# Revit family: Edge_TB42_E_Side_Hung_Standard
name_source: partatom
category: Windows
revit_build: Autodesk Revit 2014 (Build: 20130308_1515(x64)
units: mm (PartAtom-declared; Revit-internal decimal feet)

## types (18) — shared parameters
Aluminium Thickness = 1 mm  [stored 0.00328084 ft]
Area Pane Left Top = 0.52 m²
Bead SG Gap = 13 mm
Casement Dimension = 42 mm  [stored 0.137795 ft]
Custom Sash Height = 1154 mm  [stored 3.78609 ft]
Custom Sash Width = 554 mm  [stored 1.81759 ft]
DG Extrusion Start = 11 mm  [stored 0.0360892 ft]
DG Gasket Finish = Double Glazing Gasket Material
DG Thickness Calc = 4 mm  [stored 0.0131234 ft]
Default Sill Height = 800 mm  [stored 2.62467 ft]
Depth Bead = 28 mm  [stored 0.0918635 ft]
Description = Thermal break casement windows (42mm), Type E side hung
Frame Center Offset = 21 mm  [stored 0.0688976 ft]
Height Panel 1 = 1139 mm  [stored 3.73688 ft]
Height Sash = 1124 mm  [stored 3.68766 ft]
Height Sash Opening = 1154 mm  [stored 3.78609 ft]
Length Transom = 540 mm  [stored 1.77165 ft]
Limit Fixed Pane Height Max = 1800 mm
Limit Fixed Pane Height Min = 200 mm  [stored 0.656168 ft]
Limit Fixed Pane Width Max = 1500 mm  [stored 4.92126 ft]
Limit Fixed Pane Width Min = 200 mm  [stored 0.656168 ft]
Limit Sash Height Max = 1500 mm  [stored 4.92126 ft]
Limit Sash Height Min = 300 mm  [stored 0.984252 ft]
Limit Sash Width Max = 700 mm  [stored 2.29659 ft]
Limit Sash Width Min = 300 mm  [stored 0.984252 ft]
Limit Window Height Max = 1860 mm
Limit Window Height Min = 1430 mm  [stored 4.6916 ft]
Limit Window Width Max = 2130 mm
Limit Window Width Min = 830 mm  [stored 2.7231 ft]
Manufacturer = Crealco
Max System DG One Piece Thickness = 6 mm  [stored 0.019685 ft]
Max System DG Unit Thickness = 25 mm  [stored 0.082021 ft]
Model = Edge
Offset Bead SG Center Reversed = 21 mm  [stored 0.0688976 ft]
Offset Mullion Left = 570 mm  [stored 1.87008 ft]
Offset Panel 3 Bead Top = 1200 mm
Offset Panel 4 Left = 600 mm  [stored 1.9685 ft]
Offset Sash Left = 23 mm  [stored 0.0754593 ft]
Offset Sash Top = 23 mm  [stored 0.0754593 ft]
Offset Transom Top = 1170 mm
Offset Window Exterior = 21 mm  [stored 0.0688976 ft]
SG Gasket Thickness = 6 mm  [stored 0.019685 ft]
Sash Center Offset = 18 mm
Sash Overlap = 7 mm  [stored 0.0229659 ft]
Sash Spacing Inner = 8 mm  [stored 0.0262467 ft]
URL = http://www.crealco.co.za
Wall Closure = By host
Width Bead = 15 mm  [stored 0.0492126 ft]
Width Fixed Pane Bottom LHS = 540 mm  [stored 1.77165 ft]
Width Panel 1 = 540 mm  [stored 1.77165 ft]
Width Profile = 30 mm  [stored 0.0984252 ft]
Width Sash = 524 mm  [stored 1.71916 ft]
Width Sash Opening = 554 mm  [stored 1.81759 ft]
zero-valued in all types: Window Exterior Offset

## per-type parameters (varying)
- EDGE-0915S-1000Pa: Area Pane Left Bottom=0.13 m²; Area Pane Right=0.36 m²; Clearvue Insulated LowE SHGC Value=0.483; Clearvue Insulated LowE U Value=2.84; Clearvue Insulated SHGC Value=0.531; Clearvue Insulated U Value=3.33; Clearvue SHGC Value=0.588; Clearvue U Value=5.75; Custom Windload=1000 mm  [stored 3.28084 ft]; Custom Window Height=1490 mm  [stored 4.88845 ft]; Custom Window Width=890 mm  [stored 2.91995 ft]; Depth Mullion=0 mm  [stored 0 ft]; Energy Advantage SHGC Value=0.526; Energy Advantage U Value=4.33; Has Stiffener Cap=No; Height=1490 mm  [stored 4.88845 ft]; Height Fixed Pane Bottom LHS=260 mm  [stored 0.853018 ft]; Height Fixed Pane RHS=1430 mm  [stored 4.6916 ft]; Intruderprufe Insulated LowE SHGC Value=0.441; Intruderprufe Insulated LowE U Value=2.79; Intruderprufe Insulated SHGC Value=0.486; Intruderprufe Insulated U Value=3.29; Intruderprufe LowE SHGC Value=0.492; Intruderprufe LowE U Value=4.33; Intruderprufe SHGC Value=0.547; Intruderprufe U Value=5.64; Length Mullion=1490 mm  [stored 4.88845 ft]; Max Pane Area=0.52 m²; Mullion Depth Windload Based=0 mm  [stored 0 ft]; Width=890 mm  [stored 2.91995 ft]; Width Fixed Pane RHS=260 mm  [stored 0.853018 ft]; Windload Design=1000 mm  [stored 3.28084 ft]
- EDGE-1215S-1000Pa: Area Pane Left Bottom=0.13 m²; Area Pane Right=0.78 m²; Clearvue Insulated LowE SHGC Value=0.608; Clearvue Insulated LowE U Value=2.42; Clearvue Insulated SHGC Value=0.67; Clearvue Insulated U Value=3.02; Clearvue SHGC Value=0.747; Clearvue U Value=5.63; Custom Windload=1000 mm  [stored 3.28084 ft]; Custom Window Height=1490 mm  [stored 4.88845 ft]; Custom Window Width=1190 mm  [stored 3.9042 ft]; Depth Mullion=1 mm  [stored 0.00328084 ft]; Energy Advantage SHGC Value=0.667; Energy Advantage U Value=3.97; Has Stiffener Cap=Yes; Height=1490 mm  [stored 4.88845 ft]; Height Fixed Pane Bottom LHS=260 mm  [stored 0.853018 ft]; Height Fixed Pane RHS=1430 mm  [stored 4.6916 ft]; Intruderprufe Insulated LowE SHGC Value=0.556; Intruderprufe Insulated LowE U Value=2.38; Intruderprufe Insulated SHGC Value=0.615; Intruderprufe Insulated U Value=2.97; Intruderprufe LowE SHGC Value=0.621; Intruderprufe LowE U Value=3.94; Intruderprufe SHGC Value=0.698; Intruderprufe U Value=5.52; Length Mullion=1490 mm  [stored 4.88845 ft]; Max Pane Area=0.78 m²; Mullion Depth Windload Based=1 mm  [stored 0.00328084 ft]; Width=1190 mm  [stored 3.9042 ft]; Width Fixed Pane RHS=560 mm; Windload Design=1000 mm  [stored 3.28084 ft]
- EDGE-1515S-1000Pa: Area Pane Left Bottom=0.13 m²; Area Pane Right=1.21 m²; Clearvue Insulated LowE SHGC Value=0.644; Clearvue Insulated LowE U Value=2.45; Clearvue Insulated SHGC Value=0.709; Clearvue Insulated U Value=3.11; Clearvue SHGC Value=0.792; Clearvue U Value=5.93; Custom Windload=1000 mm  [stored 3.28084 ft]; Custom Window Height=1490 mm  [stored 4.88845 ft]; Custom Window Width=1490 mm  [stored 4.88845 ft]; Depth Mullion=1 mm  [stored 0.00328084 ft]; Energy Advantage SHGC Value=0.708; Energy Advantage U Value=4.11; Has Stiffener Cap=Yes; Height=1490 mm  [stored 4.88845 ft]; Height Fixed Pane Bottom LHS=260 mm  [stored 0.853018 ft]; Height Fixed Pane RHS=1430 mm  [stored 4.6916 ft]; Intruderprufe Insulated LowE SHGC Value=0.589; Intruderprufe Insulated LowE U Value=2.4; Intruderprufe Insulated SHGC Value=0.651; Intruderprufe Insulated U Value=3.06; Intruderprufe LowE SHGC Value=0.659; Intruderprufe LowE U Value=4.07; Intruderprufe SHGC Value=0.741; Intruderprufe U Value=5.81; Length Mullion=1490 mm  [stored 4.88845 ft]; Max Pane Area=1.21 m²; Mullion Depth Windload Based=1 mm  [stored 0.00328084 ft]; Width=1490 mm  [stored 4.88845 ft]; Width Fixed Pane RHS=860 mm  [stored 2.82152 ft]; Windload Design=1000 mm  [stored 3.28084 ft]
- EDGE-0918S-1000Pa: Area Pane Left Bottom=0.29 m²; Area Pane Right=0.43 m²; Clearvue Insulated LowE SHGC Value=0.593; Clearvue Insulated LowE U Value=2.48; Clearvue Insulated SHGC Value=0.653; Clearvue Insulated U Value=3.03; Clearvue SHGC Value=0.725; Clearvue U Value=5.51; Custom Windload=1000 mm  [stored 3.28084 ft]; Custom Window Height=1790 mm; Custom Window Width=890 mm  [stored 2.91995 ft]; Depth Mullion=1 mm  [stored 0.00328084 ft]; Energy Advantage SHGC Value=0.648; Energy Advantage U Value=3.97; Has Stiffener Cap=Yes; Height=1790 mm; Height Fixed Pane Bottom LHS=560 mm; Height Fixed Pane RHS=1730 mm; Intruderprufe Insulated LowE SHGC Value=0.542; Intruderprufe Insulated LowE U Value=2.44; Intruderprufe Insulated SHGC Value=0.599; Intruderprufe Insulated U Value=2.99; Intruderprufe LowE SHGC Value=0.603; Intruderprufe LowE U Value=3.94; Intruderprufe SHGC Value=0.677; Intruderprufe U Value=5.4; Length Mullion=1790 mm; Max Pane Area=0.52 m²; Mullion Depth Windload Based=1 mm  [stored 0.00328084 ft]; Width=890 mm  [stored 2.91995 ft]; Width Fixed Pane RHS=260 mm  [stored 0.853018 ft]; Windload Design=1000 mm  [stored 3.28084 ft]
- EDGE-1218S-1000Pa: Area Pane Left Bottom=0.29 m²; Area Pane Right=0.95 m²; Clearvue Insulated LowE SHGC Value=0.67; Clearvue Insulated LowE U Value=2.59; Clearvue Insulated SHGC Value=0.737; Clearvue Insulated U Value=3.27; Clearvue SHGC Value=0.822; Clearvue U Value=6.16; Custom Windload=1000 mm  [stored 3.28084 ft]; Custom Window Height=1790 mm; Custom Window Width=1190 mm  [stored 3.9042 ft]; Depth Mullion=1 mm  [stored 0.00328084 ft]; Energy Advantage SHGC Value=0.735; Energy Advantage U Value=4.31; Has Stiffener Cap=Yes; Height=1790 mm; Height Fixed Pane Bottom LHS=560 mm; Height Fixed Pane RHS=1730 mm; Intruderprufe Insulated LowE SHGC Value=0.613; Intruderprufe Insulated LowE U Value=2.55; Intruderprufe Insulated SHGC Value=0.677; Intruderprufe Insulated U Value=3.21; Intruderprufe LowE SHGC Value=0.684; Intruderprufe LowE U Value=4.27; Intruderprufe SHGC Value=0.77; Intruderprufe U Value=6.04; Length Mullion=1790 mm; Max Pane Area=0.95 m²; Mullion Depth Windload Based=1 mm  [stored 0.00328084 ft]; Width=1190 mm  [stored 3.9042 ft]; Width Fixed Pane RHS=560 mm; Windload Design=1000 mm  [stored 3.28084 ft]
- EDGE-1518S-1000Pa: Area Pane Left Bottom=0.29 m²; Area Pane Right=1.46 m²; Clearvue Insulated LowE SHGC Value=0.721; Clearvue Insulated LowE U Value=2.67; Clearvue Insulated SHGC Value=0.793; Clearvue Insulated U Value=3.42; Clearvue SHGC Value=0; Clearvue U Value=7.9; Custom Windload=1000 mm  [stored 3.28084 ft]; Custom Window Height=1790 mm; Custom Window Width=1490 mm  [stored 4.88845 ft]; Depth Mullion=1 mm  [stored 0.00328084 ft]; Energy Advantage SHGC Value=0; Energy Advantage U Value=7.9; Has Stiffener Cap=Yes; Height=1790 mm; Height Fixed Pane Bottom LHS=560 mm; Height Fixed Pane RHS=1730 mm; Intruderprufe Insulated LowE SHGC Value=0.659; Intruderprufe Insulated LowE U Value=2.62; Intruderprufe Insulated SHGC Value=0.729; Intruderprufe Insulated U Value=3.36; Intruderprufe LowE SHGC Value=0.738; Intruderprufe LowE U Value=4.49; Intruderprufe SHGC Value=0.831; Intruderprufe U Value=6.46; Length Mullion=1790 mm; Max Pane Area=1.46 m²; Mullion Depth Windload Based=1 mm  [stored 0.00328084 ft]; Width=1490 mm  [stored 4.88845 ft]; Width Fixed Pane RHS=860 mm  [stored 2.82152 ft]; Windload Design=1000 mm  [stored 3.28084 ft]
- EDGE-0915S-1500Pa: Area Pane Left Bottom=0.13 m²; Area Pane Right=0.36 m²; Clearvue Insulated LowE SHGC Value=0.553; Clearvue Insulated LowE U Value=2.38; Clearvue Insulated SHGC Value=0.608; Clearvue Insulated U Value=2.88; Clearvue SHGC Value=0.675; Clearvue U Value=5.16; Custom Windload=1500 mm  [stored 4.92126 ft]; Custom Window Height=1490 mm  [stored 4.88845 ft]; Custom Window Width=890 mm  [stored 2.91995 ft]; Depth Mullion=1 mm  [stored 0.00328084 ft]; Energy Advantage SHGC Value=0.603; Energy Advantage U Value=3.75; Has Stiffener Cap=Yes; Height=1490 mm  [stored 4.88845 ft]; Height Fixed Pane Bottom LHS=260 mm  [stored 0.853018 ft]; Height Fixed Pane RHS=1430 mm  [stored 4.6916 ft]; Intruderprufe Insulated LowE SHGC Value=0.505; Intruderprufe Insulated LowE U Value=2.33; Intruderprufe Insulated SHGC Value=0.558; Intruderprufe Insulated U Value=2.84; Intruderprufe LowE SHGC Value=0.562; Intruderprufe LowE U Value=3.73; Intruderprufe SHGC Value=0.63; Intruderprufe U Value=5.06; Length Mullion=1490 mm  [stored 4.88845 ft]; Max Pane Area=0.52 m²; Mullion Depth Windload Based=1 mm  [stored 0.00328084 ft]; Width=890 mm  [stored 2.91995 ft]; Width Fixed Pane RHS=260 mm  [stored 0.853018 ft]; Windload Design=1500 mm  [stored 4.92126 ft]
- EDGE-0915S-2000Pa: Area Pane Left Bottom=0.13 m²; Area Pane Right=0.36 m²; Clearvue Insulated LowE SHGC Value=0.553; Clearvue Insulated LowE U Value=2.38; Clearvue Insulated SHGC Value=0.608; Clearvue Insulated U Value=2.88; Clearvue SHGC Value=0.675; Clearvue U Value=5.16; Custom Windload=2000 mm; Custom Window Height=1490 mm  [stored 4.88845 ft]; Custom Window Width=890 mm  [stored 2.91995 ft]; Depth Mullion=1 mm  [stored 0.00328084 ft]; Energy Advantage SHGC Value=0.603; Energy Advantage U Value=3.75; Has Stiffener Cap=Yes; Height=1490 mm  [stored 4.88845 ft]; Height Fixed Pane Bottom LHS=260 mm  [stored 0.853018 ft]; Height Fixed Pane RHS=1430 mm  [stored 4.6916 ft]; Intruderprufe Insulated LowE SHGC Value=0.505; Intruderprufe Insulated LowE U Value=2.33; Intruderprufe Insulated SHGC Value=0.558; Intruderprufe Insulated U Value=2.84; Intruderprufe LowE SHGC Value=0.562; Intruderprufe LowE U Value=3.73; Intruderprufe SHGC Value=0.63; Intruderprufe U Value=5.06; Length Mullion=1490 mm  [stored 4.88845 ft]; Max Pane Area=0.52 m²; Mullion Depth Windload Based=1 mm  [stored 0.00328084 ft]; Width=890 mm  [stored 2.91995 ft]; Width Fixed Pane RHS=260 mm  [stored 0.853018 ft]; Windload Design=2000 mm
- EDGE-1215S-1500Pa: Area Pane Left Bottom=0.13 m²; Area Pane Right=0.78 m²; Clearvue Insulated LowE SHGC Value=0.608; Clearvue Insulated LowE U Value=2.42; Clearvue Insulated SHGC Value=0.67; Clearvue Insulated U Value=3.02; Clearvue SHGC Value=0.747; Clearvue U Value=5.63; Custom Windload=1500 mm  [stored 4.92126 ft]; Custom Window Height=1490 mm  [stored 4.88845 ft]; Custom Window Width=1190 mm  [stored 3.9042 ft]; Depth Mullion=1 mm  [stored 0.00328084 ft]; Energy Advantage SHGC Value=0.667; Energy Advantage U Value=3.97; Has Stiffener Cap=Yes; Height=1490 mm  [stored 4.88845 ft]; Height Fixed Pane Bottom LHS=260 mm  [stored 0.853018 ft]; Height Fixed Pane RHS=1430 mm  [stored 4.6916 ft]; Intruderprufe Insulated LowE SHGC Value=0.556; Intruderprufe Insulated LowE U Value=2.38; Intruderprufe Insulated SHGC Value=0.615; Intruderprufe Insulated U Value=2.97; Intruderprufe LowE SHGC Value=0.621; Intruderprufe LowE U Value=3.94; Intruderprufe SHGC Value=0.698; Intruderprufe U Value=5.52; Length Mullion=1490 mm  [stored 4.88845 ft]; Max Pane Area=0.78 m²; Mullion Depth Windload Based=1 mm  [stored 0.00328084 ft]; Width=1190 mm  [stored 3.9042 ft]; Width Fixed Pane RHS=560 mm; Windload Design=1500 mm  [stored 4.92126 ft]
- EDGE-1215S-2000Pa: Area Pane Left Bottom=0.13 m²; Area Pane Right=0.78 m²; Clearvue Insulated LowE SHGC Value=0.608; Clearvue Insulated LowE U Value=2.42; Clearvue Insulated SHGC Value=0.67; Clearvue Insulated U Value=3.02; Clearvue SHGC Value=0.747; Clearvue U Value=5.63; Custom Windload=2000 mm; Custom Window Height=1490 mm  [stored 4.88845 ft]; Custom Window Width=1190 mm  [stored 3.9042 ft]; Depth Mullion=1 mm  [stored 0.00328084 ft]; Energy Advantage SHGC Value=0.667; Energy Advantage U Value=3.97; Has Stiffener Cap=Yes; Height=1490 mm  [stored 4.88845 ft]; Height Fixed Pane Bottom LHS=260 mm  [stored 0.853018 ft]; Height Fixed Pane RHS=1430 mm  [stored 4.6916 ft]; Intruderprufe Insulated LowE SHGC Value=0.556; Intruderprufe Insulated LowE U Value=2.38; Intruderprufe Insulated SHGC Value=0.615; Intruderprufe Insulated U Value=2.97; Intruderprufe LowE SHGC Value=0.621; Intruderprufe LowE U Value=3.94; Intruderprufe SHGC Value=0.698; Intruderprufe U Value=5.52; Length Mullion=1490 mm  [stored 4.88845 ft]; Max Pane Area=0.78 m²; Mullion Depth Windload Based=1 mm  [stored 0.00328084 ft]; Width=1190 mm  [stored 3.9042 ft]; Width Fixed Pane RHS=560 mm; Windload Design=2000 mm
- EDGE-1515S-1500Pa: Area Pane Left Bottom=0.13 m²; Area Pane Right=1.21 m²; Clearvue Insulated LowE SHGC Value=0.644; Clearvue Insulated LowE U Value=2.45; Clearvue Insulated SHGC Value=0.709; Clearvue Insulated U Value=3.11; Clearvue SHGC Value=0.792; Clearvue U Value=5.93; Custom Windload=1500 mm  [stored 4.92126 ft]; Custom Window Height=1490 mm  [stored 4.88845 ft]; Custom Window Width=1490 mm  [stored 4.88845 ft]; Depth Mullion=1 mm  [stored 0.00328084 ft]; Energy Advantage SHGC Value=0.708; Energy Advantage U Value=4.11; Has Stiffener Cap=Yes; Height=1490 mm  [stored 4.88845 ft]; Height Fixed Pane Bottom LHS=260 mm  [stored 0.853018 ft]; Height Fixed Pane RHS=1430 mm  [stored 4.6916 ft]; Intruderprufe Insulated LowE SHGC Value=0.589; Intruderprufe Insulated LowE U Value=2.4; Intruderprufe Insulated SHGC Value=0.651; Intruderprufe Insulated U Value=3.06; Intruderprufe LowE SHGC Value=0.659; Intruderprufe LowE U Value=4.07; Intruderprufe SHGC Value=0.741; Intruderprufe U Value=5.81; Length Mullion=1490 mm  [stored 4.88845 ft]; Max Pane Area=1.21 m²; Mullion Depth Windload Based=1 mm  [stored 0.00328084 ft]; Width=1490 mm  [stored 4.88845 ft]; Width Fixed Pane RHS=860 mm  [stored 2.82152 ft]; Windload Design=1500 mm  [stored 4.92126 ft]
- EDGE-1515S-2000Pa: Area Pane Left Bottom=0.13 m²; Area Pane Right=1.21 m²; Clearvue Insulated LowE SHGC Value=0.644; Clearvue Insulated LowE U Value=2.45; Clearvue Insulated SHGC Value=0.709; Clearvue Insulated U Value=3.11; Clearvue SHGC Value=0.792; Clearvue U Value=5.93; Custom Windload=2000 mm; Custom Window Height=1490 mm  [stored 4.88845 ft]; Custom Window Width=1490 mm  [stored 4.88845 ft]; Depth Mullion=1 mm  [stored 0.00328084 ft]; Energy Advantage SHGC Value=0.708; Energy Advantage U Value=4.11; Has Stiffener Cap=Yes; Height=1490 mm  [stored 4.88845 ft]; Height Fixed Pane Bottom LHS=260 mm  [stored 0.853018 ft]; Height Fixed Pane RHS=1430 mm  [stored 4.6916 ft]; Intruderprufe Insulated LowE SHGC Value=0.589; Intruderprufe Insulated LowE U Value=2.4; Intruderprufe Insulated SHGC Value=0.651; Intruderprufe Insulated U Value=3.06; Intruderprufe LowE SHGC Value=0.659; Intruderprufe LowE U Value=4.07; Intruderprufe SHGC Value=0.741; Intruderprufe U Value=5.81; Length Mullion=1490 mm  [stored 4.88845 ft]; Max Pane Area=1.21 m²; Mullion Depth Windload Based=1 mm  [stored 0.00328084 ft]; Width=1490 mm  [stored 4.88845 ft]; Width Fixed Pane RHS=860 mm  [stored 2.82152 ft]; Windload Design=2000 mm
- EDGE-0918S-1500Pa: Area Pane Left Bottom=0.29 m²; Area Pane Right=0.43 m²; Clearvue Insulated LowE SHGC Value=0.593; Clearvue Insulated LowE U Value=2.48; Clearvue Insulated SHGC Value=0.653; Clearvue Insulated U Value=3.03; Clearvue SHGC Value=0.725; Clearvue U Value=5.51; Custom Windload=1500 mm  [stored 4.92126 ft]; Custom Window Height=1790 mm; Custom Window Width=890 mm  [stored 2.91995 ft]; Depth Mullion=1 mm  [stored 0.00328084 ft]; Energy Advantage SHGC Value=0.648; Energy Advantage U Value=3.97; Has Stiffener Cap=Yes; Height=1790 mm; Height Fixed Pane Bottom LHS=560 mm; Height Fixed Pane RHS=1730 mm; Intruderprufe Insulated LowE SHGC Value=0.542; Intruderprufe Insulated LowE U Value=2.44; Intruderprufe Insulated SHGC Value=0.599; Intruderprufe Insulated U Value=2.99; Intruderprufe LowE SHGC Value=0.603; Intruderprufe LowE U Value=3.94; Intruderprufe SHGC Value=0.677; Intruderprufe U Value=5.4; Length Mullion=1790 mm; Max Pane Area=0.52 m²; Mullion Depth Windload Based=1 mm  [stored 0.00328084 ft]; Width=890 mm  [stored 2.91995 ft]; Width Fixed Pane RHS=260 mm  [stored 0.853018 ft]; Windload Design=1500 mm  [stored 4.92126 ft]
- EDGE-0918S-2000Pa: Area Pane Left Bottom=0.29 m²; Area Pane Right=0.43 m²; Clearvue Insulated LowE SHGC Value=0.593; Clearvue Insulated LowE U Value=2.48; Clearvue Insulated SHGC Value=0.653; Clearvue Insulated U Value=3.03; Clearvue SHGC Value=0.725; Clearvue U Value=5.51; Custom Windload=2000 mm; Custom Window Height=1790 mm; Custom Window Width=890 mm  [stored 2.91995 ft]; Depth Mullion=1 mm  [stored 0.00328084 ft]; Energy Advantage SHGC Value=0.648; Energy Advantage U Value=3.97; Has Stiffener Cap=Yes; Height=1790 mm; Height Fixed Pane Bottom LHS=560 mm; Height Fixed Pane RHS=1730 mm; Intruderprufe Insulated LowE SHGC Value=0.542; Intruderprufe Insulated LowE U Value=2.44; Intruderprufe Insulated SHGC Value=0.599; Intruderprufe Insulated U Value=2.99; Intruderprufe LowE SHGC Value=0.603; Intruderprufe LowE U Value=3.94; Intruderprufe SHGC Value=0.677; Intruderprufe U Value=5.4; Length Mullion=1790 mm; Max Pane Area=0.52 m²; Mullion Depth Windload Based=1 mm  [stored 0.00328084 ft]; Width=890 mm  [stored 2.91995 ft]; Width Fixed Pane RHS=260 mm  [stored 0.853018 ft]; Windload Design=2000 mm
- EDGE-1218S-1500Pa: Area Pane Left Bottom=0.29 m²; Area Pane Right=0.95 m²; Clearvue Insulated LowE SHGC Value=0.67; Clearvue Insulated LowE U Value=2.59; Clearvue Insulated SHGC Value=0.737; Clearvue Insulated U Value=3.27; Clearvue SHGC Value=0.822; Clearvue U Value=6.16; Custom Windload=1500 mm  [stored 4.92126 ft]; Custom Window Height=1790 mm; Custom Window Width=1190 mm  [stored 3.9042 ft]; Depth Mullion=1 mm  [stored 0.00328084 ft]; Energy Advantage SHGC Value=0.735; Energy Advantage U Value=4.31; Has Stiffener Cap=Yes; Height=1790 mm; Height Fixed Pane Bottom LHS=560 mm; Height Fixed Pane RHS=1730 mm; Intruderprufe Insulated LowE SHGC Value=0.613; Intruderprufe Insulated LowE U Value=2.55; Intruderprufe Insulated SHGC Value=0.677; Intruderprufe Insulated U Value=3.21; Intruderprufe LowE SHGC Value=0.684; Intruderprufe LowE U Value=4.27; Intruderprufe SHGC Value=0.77; Intruderprufe U Value=6.04; Length Mullion=1790 mm; Max Pane Area=0.95 m²; Mullion Depth Windload Based=1 mm  [stored 0.00328084 ft]; Width=1190 mm  [stored 3.9042 ft]; Width Fixed Pane RHS=560 mm; Windload Design=1500 mm  [stored 4.92126 ft]
- EDGE-1218S-2000Pa: Area Pane Left Bottom=0.29 m²; Area Pane Right=0.95 m²; Clearvue Insulated LowE SHGC Value=0.67; Clearvue Insulated LowE U Value=2.59; Clearvue Insulated SHGC Value=0.737; Clearvue Insulated U Value=3.27; Clearvue SHGC Value=0.822; Clearvue U Value=6.16; Custom Windload=2000 mm; Custom Window Height=1790 mm; Custom Window Width=1190 mm  [stored 3.9042 ft]; Depth Mullion=1 mm  [stored 0.00328084 ft]; Energy Advantage SHGC Value=0.735; Energy Advantage U Value=4.31; Has Stiffener Cap=Yes; Height=1790 mm; Height Fixed Pane Bottom LHS=560 mm; Height Fixed Pane RHS=1730 mm; Intruderprufe Insulated LowE SHGC Value=0.613; Intruderprufe Insulated LowE U Value=2.55; Intruderprufe Insulated SHGC Value=0.677; Intruderprufe Insulated U Value=3.21; Intruderprufe LowE SHGC Value=0.684; Intruderprufe LowE U Value=4.27; Intruderprufe SHGC Value=0.77; Intruderprufe U Value=6.04; Length Mullion=1790 mm; Max Pane Area=0.95 m²; Mullion Depth Windload Based=1 mm  [stored 0.00328084 ft]; Width=1190 mm  [stored 3.9042 ft]; Width Fixed Pane RHS=560 mm; Windload Design=2000 mm
- EDGE-1518S-1500Pa: Area Pane Left Bottom=0.29 m²; Area Pane Right=1.46 m²; Clearvue Insulated LowE SHGC Value=0.721; Clearvue Insulated LowE U Value=2.67; Clearvue Insulated SHGC Value=0.793; Clearvue Insulated U Value=3.42; Clearvue SHGC Value=0; Clearvue U Value=7.9; Custom Windload=1500 mm  [stored 4.92126 ft]; Custom Window Height=1790 mm; Custom Window Width=1490 mm  [stored 4.88845 ft]; Depth Mullion=1 mm  [stored 0.00328084 ft]; Energy Advantage SHGC Value=0; Energy Advantage U Value=7.9; Has Stiffener Cap=Yes; Height=1790 mm; Height Fixed Pane Bottom LHS=560 mm; Height Fixed Pane RHS=1730 mm; Intruderprufe Insulated LowE SHGC Value=0.659; Intruderprufe Insulated LowE U Value=2.62; Intruderprufe Insulated SHGC Value=0.729; Intruderprufe Insulated U Value=3.36; Intruderprufe LowE SHGC Value=0.738; Intruderprufe LowE U Value=4.49; Intruderprufe SHGC Value=0.831; Intruderprufe U Value=6.46; Length Mullion=1790 mm; Max Pane Area=1.46 m²; Mullion Depth Windload Based=1 mm  [stored 0.00328084 ft]; Width=1490 mm  [stored 4.88845 ft]; Width Fixed Pane RHS=860 mm  [stored 2.82152 ft]; Windload Design=1500 mm  [stored 4.92126 ft]
- EDGE-1518S-2000Pa: Area Pane Left Bottom=0.29 m²; Area Pane Right=1.46 m²; Clearvue Insulated LowE SHGC Value=0.721; Clearvue Insulated LowE U Value=2.67; Clearvue Insulated SHGC Value=0.793; Clearvue Insulated U Value=3.42; Clearvue SHGC Value=0; Clearvue U Value=7.9; Custom Windload=2000 mm; Custom Window Height=1790 mm; Custom Window Width=1490 mm  [stored 4.88845 ft]; Depth Mullion=1 mm  [stored 0.00328084 ft]; Energy Advantage SHGC Value=0; Energy Advantage U Value=7.9; Has Stiffener Cap=Yes; Height=1790 mm; Height Fixed Pane Bottom LHS=560 mm; Height Fixed Pane RHS=1730 mm; Intruderprufe Insulated LowE SHGC Value=0.659; Intruderprufe Insulated LowE U Value=2.62; Intruderprufe Insulated SHGC Value=0.729; Intruderprufe Insulated U Value=3.36; Intruderprufe LowE SHGC Value=0.738; Intruderprufe LowE U Value=4.49; Intruderprufe SHGC Value=0.831; Intruderprufe U Value=6.46; Length Mullion=1790 mm; Max Pane Area=1.46 m²; Mullion Depth Windload Based=1 mm  [stored 0.00328084 ft]; Width=1490 mm  [stored 4.88845 ft]; Width Fixed Pane RHS=860 mm  [stored 2.82152 ft]; Windload Design=2000 mm

note: [stored X ft] marks values corroborated as IEEE doubles in the binary element streams (Revit-internal decimal feet)

## geometry (parser evidence)
native form markers: Blend x4, Extrusion x1, Sweep x28
no freeform markers — native parametric forms only
